# Revit family: is_3360_058197
name_source: partatom
category: Elektroinstallationen
revit_build: Autodesk Revit 2016 (Build: 20190508_0715(x64)
units: mm (PartAtom-declared; Revit-internal decimal feet)

## family parameters
Basisbauteil = Fläche
Beim Laden mit Abzugskörper schneiden = Nein
Bemaßung runder Anschluss = Durchmesser verwenden
Beschriftungsausrichtung beibehalten = Nein
Gemeinsam genutzt = Nein
Raumberechnungspunkt = Nein
Teiletyp = Normal

## types (1)
- IS 3360
    Apparent Load = 0 VA
    Beschreibung = Type: Motion and Presence Detector; Dimensions (Ø x H): 124 x 78 mm; Power supply, detail: KNX bus; Sensor Technology: passive infrared; Application, place: Indoors; Application, room: production facilities, recreation room, changing room, function room / ancillary room, sports hall, reception / lobby, stairwell, WC / washroom, multi-storey / underground car park, warehouse, Indoors; Installation site: ceiling; Installation: Concealed wiring; Switching zones: 1416 switching zones; Electronic scalability: No; Mechanical scalability: No; Mounting height: 2,50 – 4,00 m; Optimum mounting height: 2,8 m; Detection angle: 360 °; Angle of aperture: 160 °; Sneak-by guard: Yes; Capability of masking out individual segments: Yes; Reach, radial: Ø 8 m (50 m²); Reach, tangential: Ø 40 m (1257 m²); Reach, presence: Ø 3 m (7 m²); Twilight setting TEACH: Yes; Twilight setting: 2 – 1000 lx; Basic light level function: Yes; KNX functions: Photo-cell controller, Basic light level function, Light level, HVAC output, Constant-lighting control, Light output 2x, Day / night function, Presence output; With bus coupling: Yes; Settings via: ETS software, Remote control, Bus, Smart Remote; IP-rating: IP20; Material: Plastic; Ambient temperature: -20 – 50 °C; Colour: white; Manufacturer's Warranty: 5 years; Version: KNX - concealed, rd. white; PU1, EAN: 4007841058197
    Height = 0 mm  [stored 0 ft]
    Hersteller = Steinel
    Length = 124 mm  [stored 0.406824 ft]
    Maximum range = 20.158 m
    ModVariant = Nein
    Modell = 058197
    Mounting Place = Ceiling
    Mounting Type = Recessed
    Number of Poles = 1
    OnlyDefault = Ja
    Power Factor = 1
    Product Name = IS 3360
    Product group = Presence detector
    ProductGroupID = 4
    Protection Class = Protection class
    Protection Degree = IP 20
    RlxData = <blob elided: 178057 chars, md5=2a5823fa>
    Sensor characteristics = Circular 300°-360°
    Sensor type = Passive (infrared)
    SensorDataFile = <blob elided: 6785 chars, md5=23016e95>
    Type of entry = Presence, Motion
    Typenbild = produkt1_058197.jpg
    Typenkommentare = Product without accessories
    URL = http://relux.com
    VarID = ---
    Voltage = 0 V
    Vorgabe-Ansicht = 1800 mm
    Weight = 0.00 kg
    Width = 0 mm  [stored 0 ft]

note: [stored X ft] marks values corroborated as IEEE doubles in the binary element streams (Revit-internal decimal feet)

## geometry (parser evidence)
native form markers: Blend x4, Sweep x17
no freeform markers — native parametric forms only
